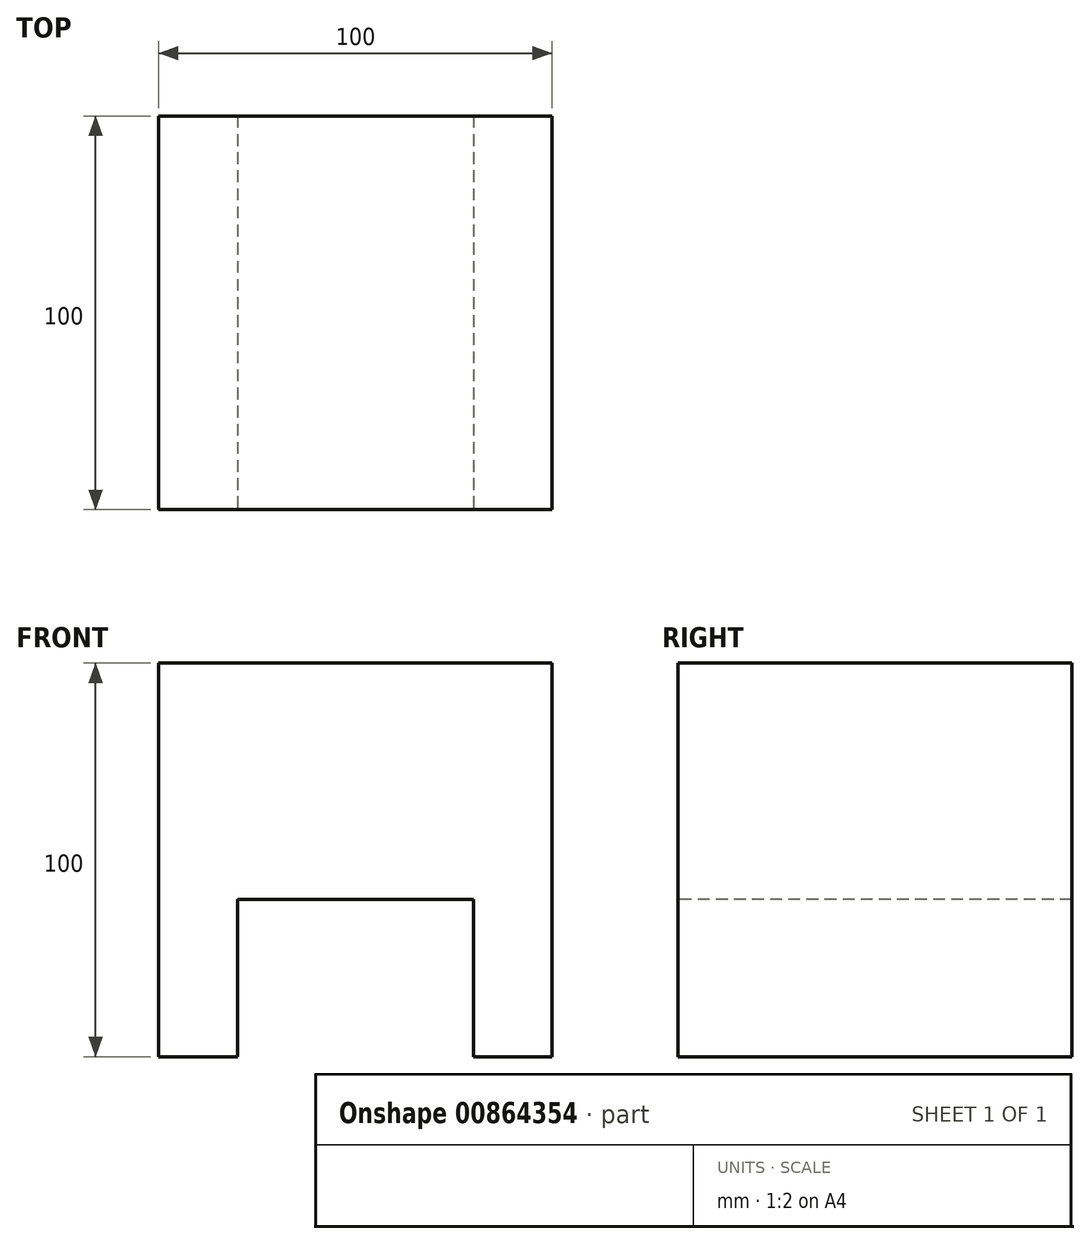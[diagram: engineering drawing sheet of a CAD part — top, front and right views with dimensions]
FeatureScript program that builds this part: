
annotation { "Feature Type Name" : "Feature", "Feature Type Description" : "" }
export const myFeature = defineFeature(function(context is Context, id is Id, definition is map)
    precondition{}
    {
        {
            var Q0;
            Q0=qCreatedBy(makeId("Top.planeOp"),FACE);
            var sketch = newSketch(context, id + "F0", { "sketchPlane" : qUnion([Q0])});
            skLineSegment(sketch, "E0.bottom", {"start": v(50, -50) * mm, "end": v(-50, -50) * mm});
            skLineSegment(sketch, "E0.top", {"start": v(50, 50) * mm, "end": v(-50, 50) * mm});
            skLineSegment(sketch, "E0.left", {"start": v(50, -50) * mm, "end": v(50, 50) * mm});
            skLineSegment(sketch, "E0.right", {"start": v(-50, -50) * mm, "end": v(-50, 50) * mm});
            skPoint(sketch, "E0.middle", {"position": v(0, 0) * mm});
            skSolve(sketch);
        }
        {
            var Q0;
            Q0=makeQuery(id+"F0.imprint","IMPRINT",FACE,{"disambiguationData":[TD([[makeQuery(id+"F0.imprint","IMPRINT",EDGE,{"derivedFrom":sQuery(id+"F0.wireOp",EDGE,"E0.bottom")}),-1.0]])]});
            extrude(context, id + "F1", {"entities" : qUnion([Q0]), "depth" : 100 * mm, "offsetDistance" : 25 * mm});
        }
        {
            var Q0;
            Q0=makeQuery(id+"F1.opExtrude","CAP_FACE",FACE,{"disambiguationData":[OSD([sQuery(id+"F0.wireOp",EDGE,"E0.bottom"),sQuery(id+"F0.wireOp",EDGE,"E0.top"),sQuery(id+"F0.wireOp",EDGE,"E0.left"),sQuery(id+"F0.wireOp",EDGE,"E0.right")])],"isStart":false});
            var sketch = newSketch(context, id + "F2", { "sketchPlane" : qUnion([Q0])});
            skLineSegment(sketch, "E1.bottom", {"start": v(-50, 14.8) * mm, "end": v(50, 14.8) * mm});
            skLineSegment(sketch, "E1.top", {"start": v(-50, 14.89) * mm, "end": v(50, 14.89) * mm});
            skLineSegment(sketch, "E1.left", {"start": v(-50, 14.8) * mm, "end": v(-50, 14.89) * mm});
            skLineSegment(sketch, "E1.right", {"start": v(50, 14.8) * mm, "end": v(50, 14.89) * mm});
            skSolve(sketch);
        }
        {
            var Q0;
            {var subQ0=sQuery(id+"F2.wireOp",EDGE,"E1.bottom");Q0=makeQuery(id+"F2.imprint","IMPRINT",FACE,{"disambiguationData":[TD([[makeQuery(id+"F2.imprint","IMPRINT",EDGE,{"derivedFrom":subQ0}),-1.0]])]});}
            extrude(context, id + "F3", {"entities" : qUnion([Q0]), "operationType" : NewBodyOperationType.REMOVE, "oppositeDirection" : true, "depth" : 40 * mm, "offsetDistance" : 25 * mm});
        }
        {
            var Q0;
            Q0=makeQuery(id+"F1.opExtrude","SWEPT_FACE",FACE,{"disambiguationData":[OSD([sQuery(id+"F0.wireOp",EDGE,"E0.bottom")])]});
            var sketch = newSketch(context, id + "F4", { "sketchPlane" : qUnion([Q0])});
            skLineSegment(sketch, "E2.bottom", {"start": v(-30, 40) * mm, "end": v(30, 40) * mm});
            skLineSegment(sketch, "E2.top", {"start": v(-30, 0) * mm, "end": v(30, 0) * mm});
            skLineSegment(sketch, "E2.left", {"start": v(-30, 40) * mm, "end": v(-30, 0) * mm});
            skLineSegment(sketch, "E2.right", {"start": v(30, 40) * mm, "end": v(30, 0) * mm});
            skSolve(sketch);
        }
        {
            var Q0;
            Q0=makeQuery(id+"F4.imprint","IMPRINT",FACE,{"disambiguationData":[TD([[makeQuery(id+"F4.imprint","IMPRINT",EDGE,{"derivedFrom":sQuery(id+"F4.wireOp",EDGE,"E2.bottom")}),-1.0]])]});
            extrude(context, id + "F5", {"entities" : qUnion([Q0]), "operationType" : NewBodyOperationType.REMOVE, "endBound" : BoundingType.THROUGH_ALL, "oppositeDirection" : true, "depth" : 25 * mm, "offsetDistance" : 25 * mm});
        }
        {
            var Q0;
            Q0=makeQuery(id+"F3.boolean.opBoolean","COPY",FACE,{"derivedFrom":makeQuery(id+"F3.opExtrude","CAP_FACE",FACE,{"disambiguationData":[OSD([sQuery(id+"F0.wireOp",EDGE,"E0.bottom"),sQuery(id+"F0.wireOp",EDGE,"E0.left"),sQuery(id+"F0.wireOp",EDGE,"E0.right"),sQuery(id+"F2.wireOp",EDGE,"E1.bottom")])],"isStart":false})});
            extrude(context, id + "F6", {"entities" : qUnion([Q0]), "operationType" : NewBodyOperationType.ADD, "depth" : 40 * mm, "offsetDistance" : 25 * mm});
        }
    });
